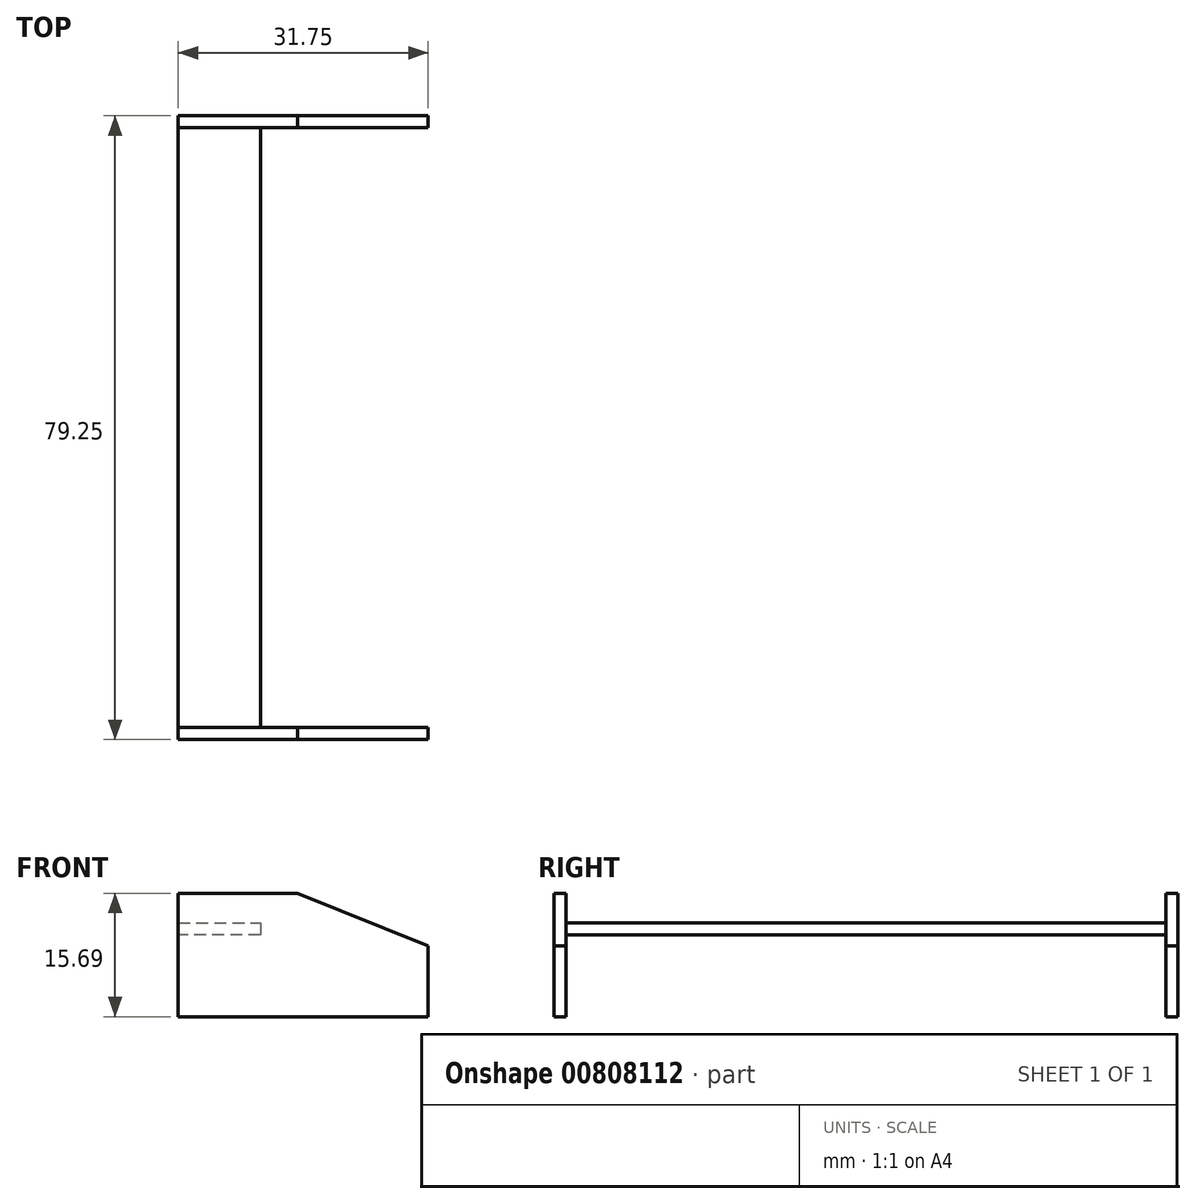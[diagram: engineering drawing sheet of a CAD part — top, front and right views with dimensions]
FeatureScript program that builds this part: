
annotation { "Feature Type Name" : "Feature", "Feature Type Description" : "" }
export const myFeature = defineFeature(function(context is Context, id is Id, definition is map)
    precondition{}
    {
        {
            var Q0;
            Q0=qCreatedBy(makeId("Front.planeOp"),FACE);
            var sketch = newSketch(context, id + "F0", { "sketchPlane" : qUnion([Q0])});
            skLineSegment(sketch, "E0", {"start": v(-13.4, 22.62) * mm, "end": v(-13.4, 6.93) * mm});
            skLineSegment(sketch, "E1", {"start": v(-13.4, 6.93) * mm, "end": v(18.35, 6.93) * mm});
            skLineSegment(sketch, "E2", {"start": v(18.35, 6.93) * mm, "end": v(18.35, 15.94) * mm});
            skLineSegment(sketch, "E3", {"start": v(18.35, 15.94) * mm, "end": v(1.76, 22.62) * mm});
            skLineSegment(sketch, "E4", {"start": v(1.76, 22.62) * mm, "end": v(-13.4, 22.62) * mm});
            skSolve(sketch);
        }
        {
            var Q0;
            Q0=qSketchRegion(id+"F0",true);
            extrude(context, id + "F1", {"entities" : qUnion([Q0]), "endBound" : BoundingType.SYMMETRIC, "oppositeDirection" : true, "depth" : 1.52 * mm, "offsetDistance" : 25.4 * mm});
        }
        {
            var Q0;
            Q0=makeQuery(id+"F1.opExtrude","CAP_FACE",FACE,{"disambiguationData":[OSD([sQuery(id+"F0.wireOp",EDGE,"E0"),sQuery(id+"F0.wireOp",EDGE,"E1"),sQuery(id+"F0.wireOp",EDGE,"E2"),sQuery(id+"F0.wireOp",EDGE,"E3"),sQuery(id+"F0.wireOp",EDGE,"E4")])],"isStart":false});
            var sketch = newSketch(context, id + "F2", { "sketchPlane" : qUnion([Q0])});
            skLineSegment(sketch, "E5", {"start": v(13.4, 18.85) * mm, "end": v(2.97, 18.85) * mm});
            skLineSegment(sketch, "E6", {"start": v(2.97, 18.85) * mm, "end": v(2.97, 17.32) * mm});
            skLineSegment(sketch, "E7", {"start": v(2.97, 17.32) * mm, "end": v(13.4, 17.32) * mm});
            skSolve(sketch);
        }
        {
            var Q0;
            {var subQ0=sQuery(id+"F2.wireOp",EDGE,"E5");Q0=makeQuery(id+"F2.imprint","IMPRINT",FACE,{"disambiguationData":[TD([[makeQuery(id+"F2.imprint","IMPRINT",EDGE,{"derivedFrom":subQ0}),1.0]])]});}
            extrude(context, id + "F3", {"entities" : qUnion([Q0]), "operationType" : NewBodyOperationType.ADD, "depth" : 38.1 * mm, "offsetDistance" : 25.4 * mm});
        }
        {
            var Q0;
            Q0=makeQuery(id+"F3.opExtrude","CAP_FACE",FACE,{"disambiguationData":[OSD([sQuery(id+"F0.wireOp",EDGE,"E0"),sQuery(id+"F2.wireOp",EDGE,"E5"),sQuery(id+"F2.wireOp",EDGE,"E6"),sQuery(id+"F2.wireOp",EDGE,"E7")])],"isStart":false});
            cPlane(context, id + "F4", {"entities" : qUnion([Q0]), "cplaneType" : CPlaneType.OFFSET, "offset" : 0 * mm, "oppositeDirection" : true, "width" : 152.4 * mm, "height" : 152.4 * mm});
        }
        {
            var Q0;
            Q0=makeQuery(id+"F1.opExtrude","SWEPT_BODY",BODY,{"disambiguationData":[OSD([sQuery(id+"F0.wireOp",EDGE,"E0"),sQuery(id+"F0.wireOp",EDGE,"E1"),sQuery(id+"F0.wireOp",EDGE,"E2"),sQuery(id+"F0.wireOp",EDGE,"E3"),sQuery(id+"F0.wireOp",EDGE,"E4")])]});
            var Q1;
            Q1=qCreatedBy(id+"F4.planeOp",FACE);
            mirror(context, id + "F5", {"operationType" : NewBodyOperationType.ADD, "entities" : qUnion([Q0]), "mirrorPlane" : qUnion([Q1])});
        }
    });
